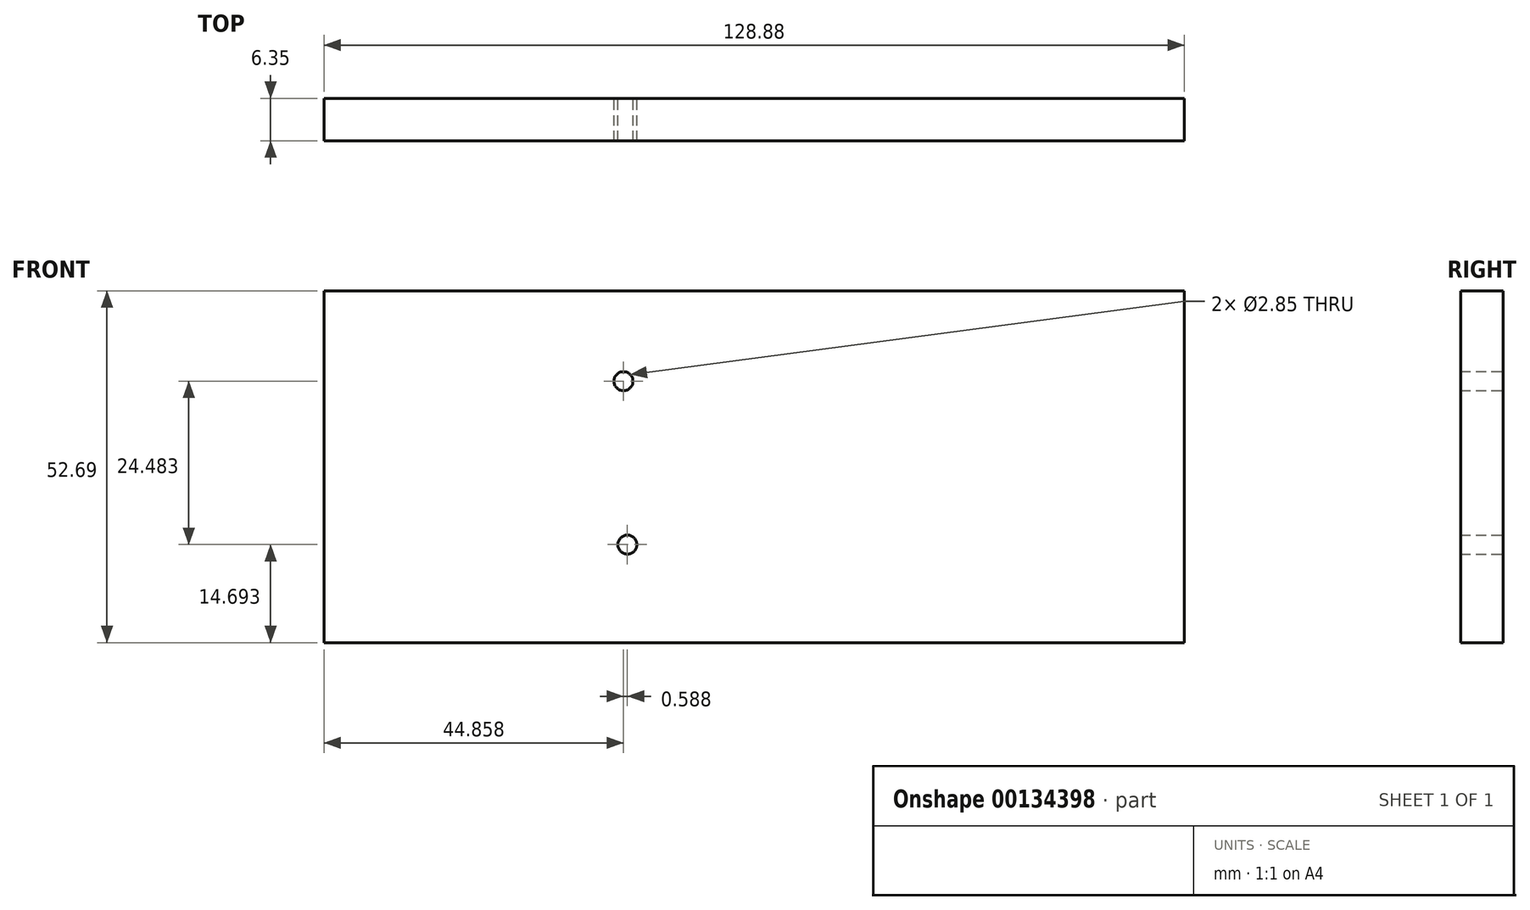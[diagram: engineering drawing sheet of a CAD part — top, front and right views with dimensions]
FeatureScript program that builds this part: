
annotation { "Feature Type Name" : "Feature", "Feature Type Description" : "" }
export const myFeature = defineFeature(function(context is Context, id is Id, definition is map)
    precondition{}
    {
        {
            var Q0;
            Q0=qCreatedBy(makeId("Front.planeOp"),FACE);
            var sketch = newSketch(context, id + "F0", { "sketchPlane" : qUnion([Q0])});
            skLineSegment(sketch, "E0.bottom", {"start": v(-64.15, 27.91) * mm, "end": v(64.73, 27.91) * mm});
            skLineSegment(sketch, "E0.top", {"start": v(-64.15, -24.78) * mm, "end": v(64.73, -24.78) * mm});
            skLineSegment(sketch, "E0.left", {"start": v(-64.15, 27.91) * mm, "end": v(-64.15, -24.78) * mm});
            skLineSegment(sketch, "E0.right", {"start": v(64.73, 27.91) * mm, "end": v(64.73, -24.78) * mm});
            skLineSegment(sketch, "E1", {"start": v(-44.56, 17.33) * mm, "end": v(-44.56, -15.96) * mm});
            skCircle(sketch, "E2", {"center": v(-19.3, 14.4) * mm, "radius": 1.43 * mm});
            skCircle(sketch, "E3", {"center": v(-18.7, -10.09) * mm, "radius": 1.43 * mm});
            skCircle(sketch, "E4", {"center": v(7.54, 0) * mm, "radius": 16.77 * mm});
            skCircle(sketch, "E5", {"center": v(45.54, 0) * mm, "radius": 16.76 * mm});
            skSolve(sketch);
        }
        {
            var Q0;
            Q0=makeQuery(id+"F0.imprint","IMPRINT",FACE,{"disambiguationData":[TD([[makeQuery(id+"F0.imprint","IMPRINT",EDGE,{"derivedFrom":sQuery(id+"F0.wireOp",EDGE,"E0.bottom")}),-1.0]])]});
            var Q1;
            Q1=makeQuery(id+"F0.imprint","IMPRINT",FACE,{"disambiguationData":[TD([[makeQuery(id+"F0.imprint","IMPRINT",EDGE,{"derivedFrom":sQuery(id+"F0.wireOp",EDGE,"E5")}),1.0]])]});
            var Q2;
            Q2=makeQuery(id+"F0.imprint","IMPRINT",FACE,{"disambiguationData":[TD([[makeQuery(id+"F0.imprint","IMPRINT",EDGE,{"derivedFrom":sQuery(id+"F0.wireOp",EDGE,"E4")}),1.0]])]});
            extrude(context, id + "F1", {"entities" : qUnion([Q0, Q1, Q2]), "depth" : 6.35 * mm});
        }
    });
